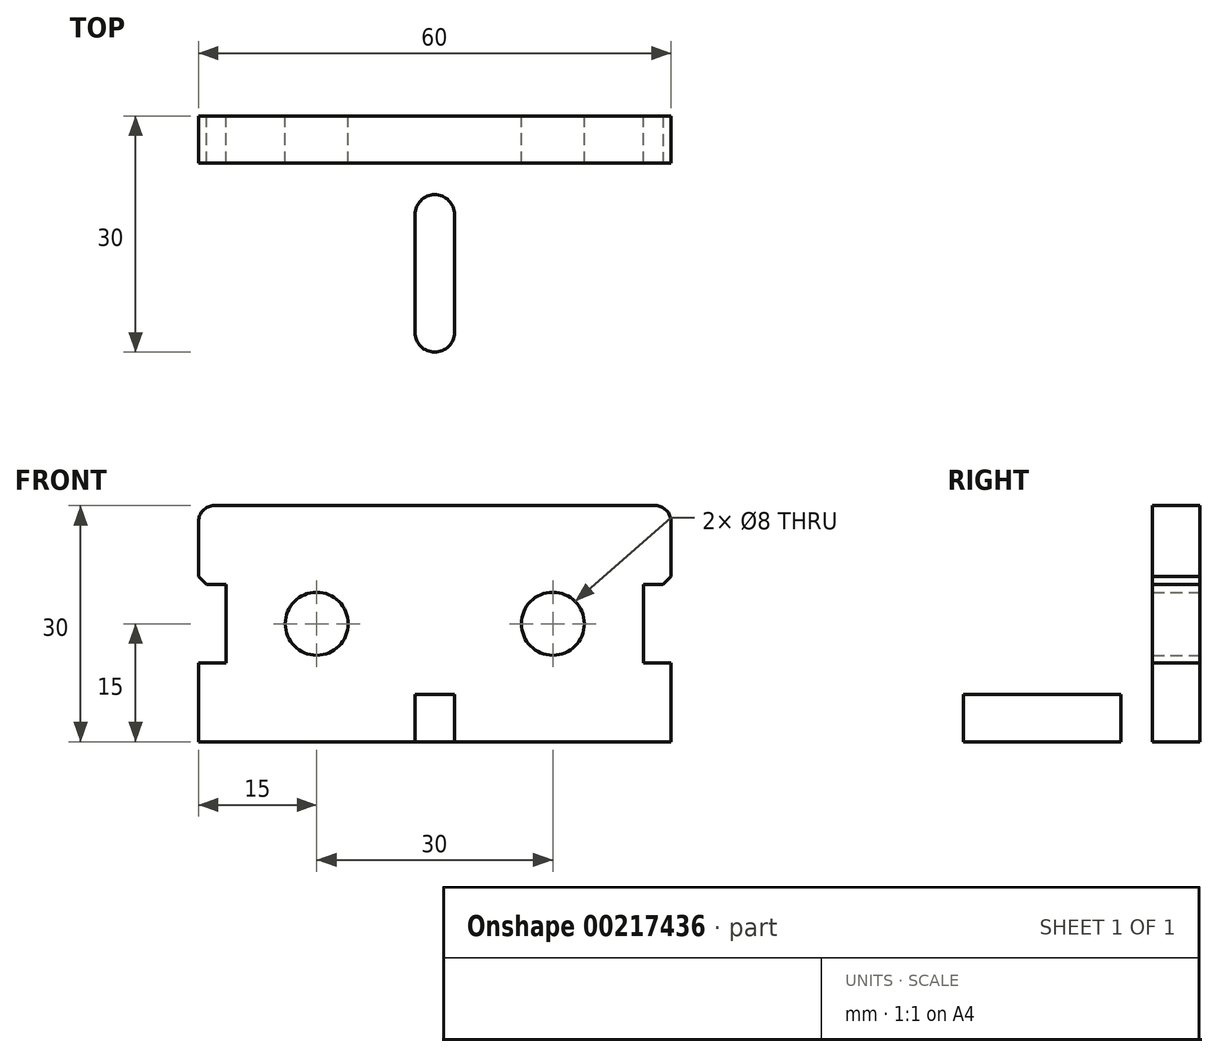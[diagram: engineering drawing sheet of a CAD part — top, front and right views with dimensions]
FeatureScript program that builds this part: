
annotation { "Feature Type Name" : "Feature", "Feature Type Description" : "" }
export const myFeature = defineFeature(function(context is Context, id is Id, definition is map)
    precondition{}
    {
        {
            var Q0;
            Q0=qCreatedBy(makeId("Right.planeOp"),FACE);
            var sketch = newSketch(context, id + "F0", { "sketchPlane" : qUnion([Q0])});
            skLineSegment(sketch, "E0", {"start": v(17.5, 0) * mm, "end": v(-17.5, 0) * mm});
            skLineSegment(sketch, "E1", {"start": v(-17.5, 0) * mm, "end": v(-17.5, 6) * mm});
            skLineSegment(sketch, "E2", {"start": v(-17.5, 6) * mm, "end": v(11.5, 6) * mm});
            skLineSegment(sketch, "E3", {"start": v(11.5, 6) * mm, "end": v(11.5, 30) * mm});
            skLineSegment(sketch, "E4", {"start": v(11.5, 30) * mm, "end": v(17.5, 30) * mm});
            skLineSegment(sketch, "E5", {"start": v(17.5, 30) * mm, "end": v(17.5, 0) * mm});
            skSolve(sketch);
        }
        {
            var Q0;
            Q0=makeQuery(id+"F0.imprint","IMPRINT",FACE,{"disambiguationData":[TD([[makeQuery(id+"F0.imprint","IMPRINT",EDGE,{"derivedFrom":sQuery(id+"F0.wireOp",EDGE,"E0")}),-1.0]])]});
            extrude(context, id + "F1", {"entities" : qUnion([Q0]), "endBound" : BoundingType.SYMMETRIC, "depth" : 60 * mm});
        }
        {
            var Q0;
            Q0=makeQuery(id+"F1.opExtrude","SWEPT_FACE",FACE,{"disambiguationData":[OSD([sQuery(id+"F0.wireOp",EDGE,"E2")])]});
            var sketch = newSketch(context, id + "F2", { "sketchPlane" : qUnion([Q0])});
            skLineSegment(sketch, "E6", {"start": v(0, 17.5) * mm, "end": v(0, -17.5) * mm, "construction": true});
            skPoint(sketch, "E7", {"position": v(-21.5, -2.5) * mm});
            skPoint(sketch, "E8", {"position": v(21.5, -2.5) * mm});
            skSolve(sketch);
        }
        {
            var Q0;
            Q0=sQuery(id+"F2.wireOp",VERTEX,"E7");
            var Q1;
            Q1=sQuery(id+"F2.wireOp",VERTEX,"E8");
            var Q2;
            Q2=makeQuery(id+"F1.opExtrude","SWEPT_BODY",BODY,{"disambiguationData":[OSD([sQuery(id+"F0.wireOp",EDGE,"E0"),sQuery(id+"F0.wireOp",EDGE,"E1"),sQuery(id+"F0.wireOp",EDGE,"E2"),sQuery(id+"F0.wireOp",EDGE,"E3"),sQuery(id+"F0.wireOp",EDGE,"E4"),sQuery(id+"F0.wireOp",EDGE,"E5")])]});
            hole(context, id + "F3", {"style" : HoleStyle.SIMPLE, "endStyle" : HoleEndStyle.THROUGH, "standardTappedOrClearance" : lookupTablePath({ "standard" : "ISO", "engagement" : "75%", "pitch" : "0.75 mm", "size" : "M4", "type" : "Tapped" }), "standardBlindInLast" : lookupTablePath({ "standard" : "ISO", "engagement" : "75%", "pitch" : "0.75 mm", "size" : "M4", "type" : "Tapped" }), "holeDiameter" : 3.2 * mm, "locations" : qUnion([Q0, Q1]), "scope" : qUnion([Q2]), "isTappedThrough" : true, "showTappedDepth" : true});
        }
        {
            var Q0;
            Q0=makeQuery(id+"F1.opExtrude","SWEPT_FACE",FACE,{"disambiguationData":[OSD([sQuery(id+"F0.wireOp",EDGE,"E5")])]});
            var sketch = newSketch(context, id + "F4", { "sketchPlane" : qUnion([Q0])});
            skCircle(sketch, "E9", {"center": v(-15, 15) * mm, "radius": 4 * mm});
            skCircle(sketch, "E10", {"center": v(15, 15) * mm, "radius": 4 * mm});
            skLineSegment(sketch, "E11", {"start": v(0, 30) * mm, "end": v(0, 0) * mm, "construction": true});
            skLineSegment(sketch, "E12", {"start": v(-30, 20) * mm, "end": v(-26.5, 20) * mm});
            skLineSegment(sketch, "E13", {"start": v(-26.5, 20) * mm, "end": v(-26.5, 10) * mm});
            skLineSegment(sketch, "E14", {"start": v(-26.5, 10) * mm, "end": v(-30, 10) * mm});
            skLineSegment(sketch, "E15", {"start": v(-30, 10) * mm, "end": v(-30, 20) * mm});
            skLineSegment(sketch, "E16", {"start": v(30, 10) * mm, "end": v(26.5, 10) * mm});
            skLineSegment(sketch, "E17", {"start": v(26.5, 10) * mm, "end": v(26.5, 20) * mm});
            skLineSegment(sketch, "E18", {"start": v(26.5, 20) * mm, "end": v(30, 20) * mm});
            skLineSegment(sketch, "E19", {"start": v(30, 20) * mm, "end": v(30, 10) * mm});
            skSolve(sketch);
        }
        {
            var Q0;
            Q0=makeQuery(id+"F4.imprint","IMPRINT",FACE,{"disambiguationData":[TD([[makeQuery(id+"F4.imprint","IMPRINT",EDGE,{"derivedFrom":sQuery(id+"F4.wireOp",EDGE,"E9")}),1.0]])]});
            var Q1;
            Q1=makeQuery(id+"F4.imprint","IMPRINT",FACE,{"disambiguationData":[TD([[makeQuery(id+"F4.imprint","IMPRINT",EDGE,{"derivedFrom":sQuery(id+"F4.wireOp",EDGE,"E10")}),1.0]])]});
            var Q2;
            Q2=makeQuery(id+"F4.imprint","IMPRINT",FACE,{"disambiguationData":[TD([[makeQuery(id+"F4.imprint","IMPRINT",EDGE,{"derivedFrom":sQuery(id+"F4.wireOp",EDGE,"E16")}),-1.0]])]});
            var Q3;
            Q3=makeQuery(id+"F4.imprint","IMPRINT",FACE,{"disambiguationData":[TD([[makeQuery(id+"F4.imprint","IMPRINT",EDGE,{"derivedFrom":sQuery(id+"F4.wireOp",EDGE,"E12")}),-1.0]])]});
            extrude(context, id + "F5", {"entities" : qUnion([Q0, Q1, Q2, Q3]), "operationType" : NewBodyOperationType.REMOVE, "endBound" : BoundingType.THROUGH_ALL, "oppositeDirection" : true, "depth" : 25 * mm});
        }
        {
            var Q0;
            Q0=makeQuery(id+"F5.boolean.opBoolean","COPY",EDGE,{"derivedFrom":makeQuery(id+"F5.opExtrude","SWEPT_EDGE",EDGE,{"disambiguationData":[OSD([sQuery(id+"F0.wireOp",EDGE,"E5"),sQuery(id+"F4.wireOp",EDGE,"E18"),sQuery(id+"F4.wireOp",EDGE,"E19")])]})});
            var Q1;
            Q1=makeQuery(id+"F5.boolean.opBoolean","COPY",EDGE,{"derivedFrom":makeQuery(id+"F5.opExtrude","SWEPT_EDGE",EDGE,{"disambiguationData":[OSD([sQuery(id+"F0.wireOp",EDGE,"E5"),sQuery(id+"F4.wireOp",EDGE,"E16"),sQuery(id+"F4.wireOp",EDGE,"E19")])]})});
            var Q2;
            Q2=makeQuery(id+"F5.boolean.opBoolean","COPY",EDGE,{"derivedFrom":makeQuery(id+"F5.opExtrude","SWEPT_EDGE",EDGE,{"disambiguationData":[OSD([sQuery(id+"F0.wireOp",EDGE,"E5"),sQuery(id+"F4.wireOp",EDGE,"E12"),sQuery(id+"F4.wireOp",EDGE,"E15")])]})});
            var Q3;
            Q3=makeQuery(id+"F5.boolean.opBoolean","COPY",EDGE,{"derivedFrom":makeQuery(id+"F5.opExtrude","SWEPT_EDGE",EDGE,{"disambiguationData":[OSD([sQuery(id+"F0.wireOp",EDGE,"E5"),sQuery(id+"F4.wireOp",EDGE,"E14"),sQuery(id+"F4.wireOp",EDGE,"E15")])]})});
            chamfer(context, id + "F6", {"entities" : qUnion([Q0, Q1, Q2, Q3]), "width" : 1 * mm, "tangentPropagation" : true});
        }
        {
            var Q0;
            Q0=makeQuery(id+"F1.opExtrude","CAP_EDGE",EDGE,{"disambiguationData":[OSD([sQuery(id+"F0.wireOp",EDGE,"E4")])],"isStart":true});
            var Q1;
            Q1=makeQuery(id+"F1.opExtrude","CAP_EDGE",EDGE,{"disambiguationData":[OSD([sQuery(id+"F0.wireOp",EDGE,"E4")])],"isStart":false});
            fillet(context, id + "F7", {"entities" : qUnion([Q0, Q1]), "radius" : 2 * mm, "tangentPropagation" : true, "allowEdgeOverflow" : false});
        }
        {
            var Q0;
            Q0=makeQuery(id+"F1.opExtrude","CAP_EDGE",EDGE,{"disambiguationData":[OSD([sQuery(id+"F0.wireOp",EDGE,"E1")])],"isStart":true});
            var Q1;
            Q1=makeQuery(id+"F1.opExtrude","CAP_EDGE",EDGE,{"disambiguationData":[OSD([sQuery(id+"F0.wireOp",EDGE,"E1")])],"isStart":false});
            fillet(context, id + "F8", {"entities" : qUnion([Q0, Q1]), "radius" : 4 * mm, "tangentPropagation" : true, "allowEdgeOverflow" : false});
        }
        {
            var Q0;
            Q0=makeQuery(id+"F1.opExtrude","SWEPT_FACE",FACE,{"disambiguationData":[OSD([sQuery(id+"F0.wireOp",EDGE,"E2")])]});
            var sketch = newSketch(context, id + "F9", { "sketchPlane" : qUnion([Q0])});
            skLineSegment(sketch, "E20", {"start": v(0, 5) * mm, "end": v(0, -10) * mm});
            skArc(sketch, "E21.0.startCap", {"start": v(-2.5, 5) * mm, "mid": v(0, 7.5) * mm, "end": v(2.5, 5) * mm});
            skArc(sketch, "E21.0.endCap", {"start": v(2.5, -10) * mm, "mid": v(0, -12.5) * mm, "end": v(-2.5, -10) * mm});
            skLineSegment(sketch, "E21.0.left", {"start": v(2.5, 5) * mm, "end": v(2.5, -10) * mm});
            skLineSegment(sketch, "E21.0.right", {"start": v(-2.5, 5) * mm, "end": v(-2.5, -10) * mm});
            skSolve(sketch);
        }
        {
            var Q0;
            Q0=makeQuery(id+"F9.imprint","IMPRINT",FACE,{"disambiguationData":[TD([[makeQuery(id+"F9.imprint","IMPRINT",EDGE,{"derivedFrom":sQuery(id+"F9.wireOp",EDGE,"E21.0.startCap")}),-1.0]])]});
            extrude(context, id + "F10", {"entities" : qUnion([Q0]), "operationType" : NewBodyOperationType.REMOVE, "endBound" : BoundingType.THROUGH_ALL, "oppositeDirection" : true, "depth" : 25 * mm});
        }
    });
